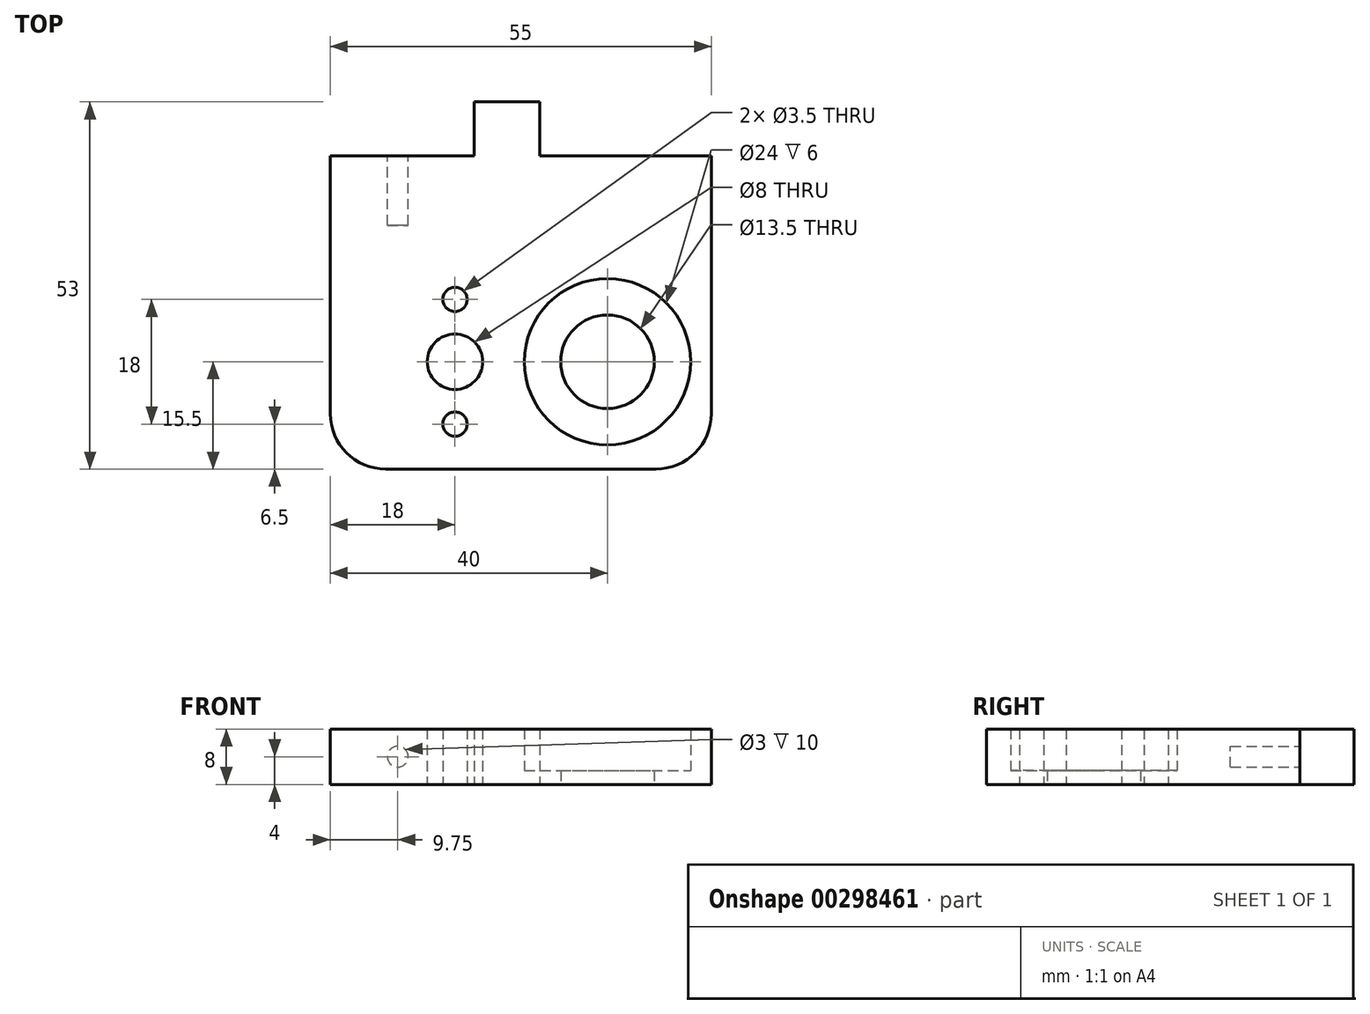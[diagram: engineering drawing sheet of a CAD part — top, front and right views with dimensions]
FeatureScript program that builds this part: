
annotation { "Feature Type Name" : "Feature", "Feature Type Description" : "" }
export const myFeature = defineFeature(function(context is Context, id is Id, definition is map)
    precondition{}
    {
        {
            var Q0;
            Q0=qCreatedBy(makeId("Top.planeOp"),FACE);
            var sketch = newSketch(context, id + "F0", { "sketchPlane" : qUnion([Q0])});
            skLineSegment(sketch, "E0.bottom", {"start": v(20.75, 0) * mm, "end": v(30.25, 0) * mm});
            skLineSegment(sketch, "E0.top", {"start": v(0, -53) * mm, "end": v(51, -53) * mm});
            skLineSegment(sketch, "E0.left", {"start": v(0, -7.8) * mm, "end": v(0, -53) * mm, "construction": true});
            skLineSegment(sketch, "E0.right", {"start": v(51, -7.8) * mm, "end": v(51, -53) * mm});
            skPoint(sketch, "E1", {"position": v(25.5, 0) * mm});
            skLineSegment(sketch, "E2.top", {"start": v(20.75, -7.8) * mm, "end": v(30.25, -7.8) * mm, "construction": true});
            skLineSegment(sketch, "E2.left", {"start": v(20.75, 0) * mm, "end": v(20.75, -7.8) * mm});
            skLineSegment(sketch, "E2.right", {"start": v(30.25, 0) * mm, "end": v(30.25, -7.8) * mm});
            skLineSegment(sketch, "E3", {"start": v(20.75, -7.8) * mm, "end": v(0, -7.8) * mm});
            skLineSegment(sketch, "E4", {"start": v(30.25, -7.8) * mm, "end": v(51, -7.8) * mm});
            skPoint(sketch, "E5.orphan", {"position": v(0, 0) * mm});
            skPoint(sketch, "E6.orphan", {"position": v(51, 0) * mm});
            skCircle(sketch, "E7", {"center": v(11, -37.5) * mm, "radius": 6.75 * mm});
            skCircle(sketch, "E8", {"center": v(33, -37.5) * mm, "radius": 4 * mm});
            skPoint(sketch, "E9.visualSharp", {"position": v(51, -53) * mm});
            skPoint(sketch, "E10.visualSharp", {"position": v(0, -53) * mm});
            skCircle(sketch, "E11", {"center": v(33, -28.5) * mm, "radius": 1.75 * mm});
            skCircle(sketch, "E12", {"center": v(33, -46.5) * mm, "radius": 1.75 * mm});
            skLineSegment(sketch, "E13", {"start": v(33, -28.5) * mm, "end": v(33, -46.5) * mm, "construction": true});
            skCircle(sketch, "E14", {"center": v(11, -37.5) * mm, "radius": 12 * mm});
            skLineSegment(sketch, "E15", {"start": v(0, -7.8) * mm, "end": v(-4, -7.8) * mm});
            skLineSegment(sketch, "E16", {"start": v(-4, -7.8) * mm, "end": v(-4, -53) * mm});
            skLineSegment(sketch, "E17", {"start": v(-4, -53) * mm, "end": v(0, -53) * mm});
            skSolve(sketch);
        }
        {
            var Q0;
            Q0=makeQuery(id+"F0.imprint","IMPRINT",FACE,{"disambiguationData":[TD([[makeQuery(id+"F0.imprint","IMPRINT",EDGE,{"derivedFrom":sQuery(id+"F0.wireOp",EDGE,"E0.top")}),1.0]])]});
            extrude(context, id + "F1", {"entities" : qUnion([Q0]), "oppositeDirection" : true, "depth" : 8 * mm});
        }
        {
            var Q0;
            Q0=makeQuery(id+"F0.imprint","IMPRINT",FACE,{"disambiguationData":[TD([[makeQuery(id+"F0.imprint","IMPRINT",EDGE,{"derivedFrom":sQuery(id+"F0.wireOp",EDGE,"E7")}),-1.0]])]});
            extrude(context, id + "F2", {"entities" : qUnion([Q0]), "operationType" : NewBodyOperationType.ADD, "oppositeDirection" : true, "depth" : 2 * mm});
        }
        {
            var Q0;
            Q0=makeQuery(id+"F1.opExtrude","SWEPT_EDGE",EDGE,{"disambiguationData":[OSD([sQuery(id+"F0.wireOp",EDGE,"E16"),sQuery(id+"F0.wireOp",EDGE,"E17")])]});
            var Q1;
            Q1=makeQuery(id+"F1.opExtrude","SWEPT_EDGE",EDGE,{"disambiguationData":[OSD([sQuery(id+"F0.wireOp",EDGE,"E0.top"),sQuery(id+"F0.wireOp",EDGE,"E0.right")])]});
            fillet(context, id + "F3", {"entities" : qUnion([Q0, Q1]), "radius" : 8 * mm, "tangentPropagation" : true, "allowEdgeOverflow" : false});
        }
        {
            var Q0;
            Q0=makeQuery(id+"F1.opExtrude","SWEPT_FACE",FACE,{"disambiguationData":[OSD([sQuery(id+"F0.wireOp",EDGE,"E4")])]});
            var sketch = newSketch(context, id + "F4", { "sketchPlane" : qUnion([Q0])});
            skLineSegment(sketch, "E18", {"start": v(-39.75, 0) * mm, "end": v(-39.75, -8) * mm, "construction": true});
            skCircle(sketch, "E19", {"center": v(-41.25, -4) * mm, "radius": 1.5 * mm});
            skPoint(sketch, "E19.centerSnap0", {"position": v(-51, -4) * mm});
            skLineSegment(sketch, "E20.bottom", {"start": v(-51, -8) * mm, "end": v(0, -8) * mm, "construction": true});
            skLineSegment(sketch, "E20.top", {"start": v(-51, 0) * mm, "end": v(0, 0) * mm, "construction": true});
            skLineSegment(sketch, "E20.left", {"start": v(-51, 0) * mm, "end": v(-51, -8) * mm, "construction": true});
            skLineSegment(sketch, "E20.right", {"start": v(0, 0) * mm, "end": v(0, -8) * mm, "construction": true});
            skLineSegment(sketch, "E21", {"start": v(-25.5, -8) * mm, "end": v(-25.5, 0) * mm, "construction": true});
            skCircle(sketch, "E22.MirrorC", {"center": v(-9.75, -4) * mm, "radius": 1.5 * mm});
            skSolve(sketch);
        }
        {
            var Q0;
            Q0=makeQuery(id+"F4.imprint","IMPRINT",FACE,{"disambiguationData":[TD([[makeQuery(id+"F4.imprint","IMPRINT",EDGE,{"derivedFrom":sQuery(id+"F4.wireOp",EDGE,"E19")}),1.0]])]});
            var Q1;
            Q1=makeQuery(id+"F4.imprint","IMPRINT",FACE,{"disambiguationData":[TD([[makeQuery(id+"F4.imprint","IMPRINT",EDGE,{"derivedFrom":sQuery(id+"F4.wireOp",EDGE,"E22.MirrorC")}),-1.0]])]});
            extrude(context, id + "F5", {"entities" : qUnion([Q0, Q1]), "operationType" : NewBodyOperationType.REMOVE, "oppositeDirection" : true, "depth" : 10 * mm});
        }
        {
            var Q0;
            Q0=makeQuery(id+"F1.opExtrude","SWEPT_BODY",BODY,{"disambiguationData":[OSD([sQuery(id+"F0.wireOp",EDGE,"E0.top"),sQuery(id+"F0.wireOp",EDGE,"E0.right"),sQuery(id+"F0.wireOp",EDGE,"E0.bottom"),sQuery(id+"F0.wireOp",EDGE,"E2.left"),sQuery(id+"F0.wireOp",EDGE,"E2.right"),sQuery(id+"F0.wireOp",EDGE,"E3"),sQuery(id+"F0.wireOp",EDGE,"E4"),sQuery(id+"F0.wireOp",EDGE,"E8"),sQuery(id+"F0.wireOp",EDGE,"E11"),sQuery(id+"F0.wireOp",EDGE,"E12"),sQuery(id+"F0.wireOp",EDGE,"E14"),sQuery(id+"F0.wireOp",EDGE,"E15"),sQuery(id+"F0.wireOp",EDGE,"E16"),sQuery(id+"F0.wireOp",EDGE,"E17")])]});
            var Q1;
            Q1=makeQuery(id+"F1.opExtrude","CAP_EDGE",EDGE,{"disambiguationData":[OSD([sQuery(id+"F0.wireOp",EDGE,"E16")])],"isStart":false});
            transform(context, id + "F6", {"entities" : qUnion([Q0]), "transformType" : TransformType.ROTATION, "transformAxis" : qUnion([Q1]), "angle" : 180 * degree, "makeCopy" : false});
        }
    });
